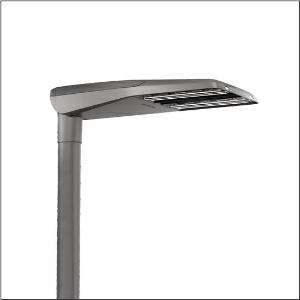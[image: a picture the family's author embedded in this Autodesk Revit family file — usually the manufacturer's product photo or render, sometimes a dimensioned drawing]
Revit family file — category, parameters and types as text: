
# Revit family: streetlight_sl_11_iq_midi___st1_2a_5xc3a41e08me_8609
name_source: partatom
category: Lighting Fixtures
units: mm (PartAtom-declared; Revit-internal decimal feet)

## family parameters
Cut with Voids When Loaded = No
Host = Face
Light Source = No
Part Type = Normal
Room Calculation Point = No
Round Connector Dimension = Use Diameter
Shared = No

## types (1)
- --- (1 x LED, 18900 lm, 124.7 W, 4000K)
    Apparent Load = 125 VA
    CIE Flux Codes = 32 70 96 100 100
    Color Rendering = 70
    Color Temperature = 4000K
    Default Elevation = 1800 mm
    Description = Streetlight SL 11 iQ midi, mast luminaire, primary light control with 3 zone facetted reflector, of plastic, silver coated, highly specular, primary optical cover: cover, of PMMA, transparent, light distribution: ST1.2a, light emission: direct distribution, primary light characteristic: asymmetric, installation type: post-top, side-entry, LED, High Power LED, rated luminous flux: 18.900lm, luminous efficacy: 152lm/W, light colour: 740, colour temperature: 4000K, control: optimised constant luminous flux control (CLO 2.0), Desk-Remote (wireless, voltage-free reading and setting of iQ features in the workshop via application-optimized NFC function/RFID function), Light-Fading, Smart-Wire, Night-Set, Lumen-Switch, Temp-Guard, Auto-Match, with cable H07RN-F 5x 1.5mm², mains connection: 230..240V, AC, 50/60Hz, connection cable pre-assembled, cable length: 12,5m, start of lifetime: 125W, end of service life: 132W, reduction: 57W, luminaire housing, of diecast aluminium, powder-coated, Siteco® metallic grey (DB 702S), please order mast flange separately, inclination adjustable without tools: 0°, 5°, 10°, 15° (post-top) | 0°, -5°, -10°, -15° (side-entry), sealing non-destructively replaceable, multi-level sealing system, length: 780mm, width: 376mm, height: 118mm, mast flange for spigot size: 42mm (side-entry): 5XC10008XM4, 60/48mm (side-entry/post-top): 5XC10108XM2, 76/60mm (side-entry/post-top): 5XC10108XM1, equipment: Power, protection rating (complete): IP66, insulation class (complete): insulation class II (safety insulation), certification: CE, ENEC, VDE, impact resistance: IK09, permissible operating ambient temperature for outdoor applications: -25..+50°C, standard-compliant lighting for roads and squares, Environmental Product Declaration (EPD) tested and certified by an independent institute, packaging unit: 1 piece

Light Distribution: ST1.2a
    Height = 118 mm
    Lamp = 1 x LED
    Lamp Light Flux = 18900 lm
    Lamp Power = 124.7 W
    Lamp count = 1
    Length = 780 mm
    Luminous efficacy = 152 lm/W
    Manufacturer = Siteco
    ModVariant = No
    Model = 5XC3A41E08ME
    Number of Poles = 1
    OnlyDefault = Yes
    Power Factor = 1
    Product Name = Streetlight SL 11 iQ midi | ST1.2a
    Product group = mast luminaire | pylon top
    ProductGroupID = 6100
    Protection Class = Protection class II
    Protection Degree = IP 66
    RLX_Detail_Level = 1
    RLX_Emergency_Light_Flux = 0 lm
    RLX_Emergency_Type = 0
    RLX_Emergency_Type_DB = No
    RlxData = <blob elided: 70817 chars, md5=51750d87>
    Socket = socket
    Standby Power = 0 W
    System Light Flux = 18900 lm
    System Power = 125 W
    Type Comments = factory setting: luminous flux: 100 % | dim-lin: 254 | 557 mA
    Type Image = l_1005960.jpg
    URL = http://relux.com
    VarID = @adj_131813
    Voltage = 0 V
    Weight = 0.00 kg
    Width = 376 mm

## geometry (parser evidence)
native form markers: Blend x4, Sweep x11
no freeform markers — native parametric forms only
